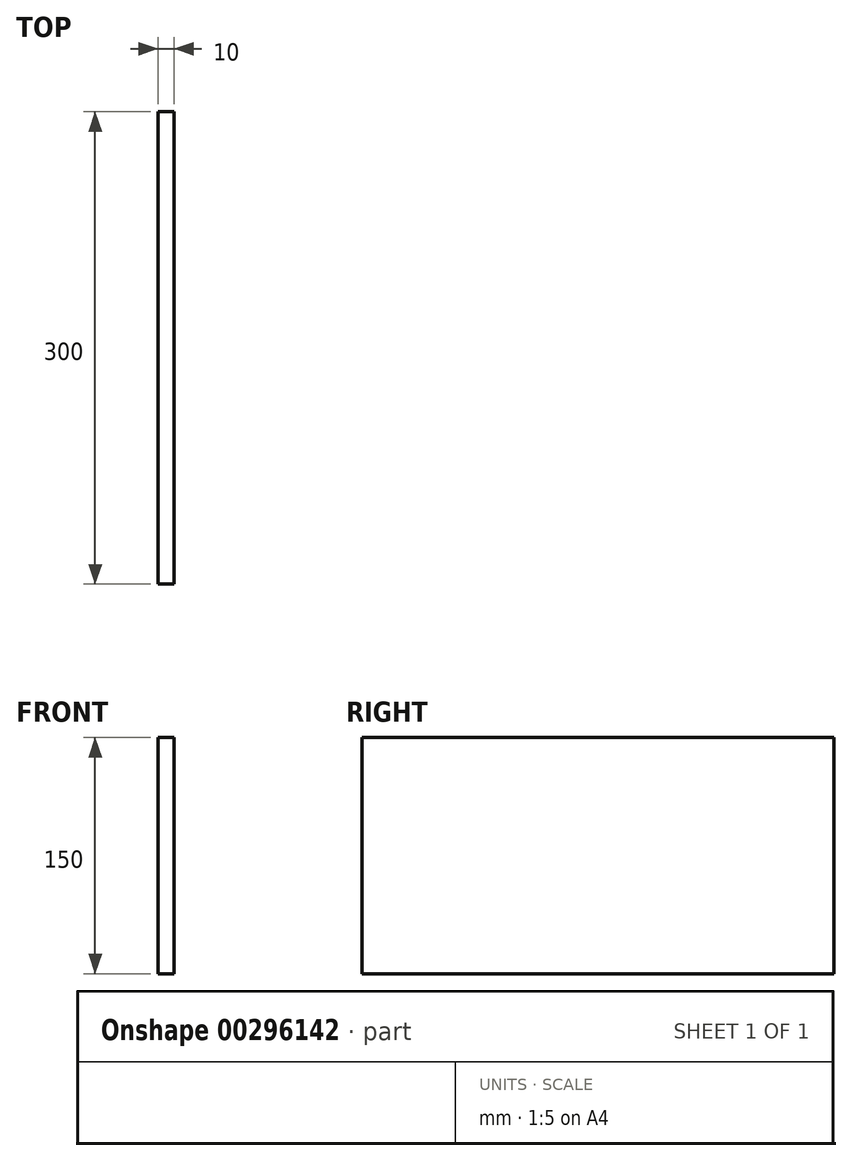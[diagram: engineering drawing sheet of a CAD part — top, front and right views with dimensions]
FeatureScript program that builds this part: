
annotation { "Feature Type Name" : "Feature", "Feature Type Description" : "" }
export const myFeature = defineFeature(function(context is Context, id is Id, definition is map)
    precondition{}
    {
        {
            var Q0;
            Q0=qCreatedBy(makeId("Front.planeOp"),FACE);
            var sketch = newSketch(context, id + "F0", { "sketchPlane" : qUnion([Q0])});
            skLineSegment(sketch, "E0.bottom", {"start": v(5, 75) * mm, "end": v(-5, 75) * mm});
            skLineSegment(sketch, "E0.top", {"start": v(5, -75) * mm, "end": v(-5, -75) * mm});
            skLineSegment(sketch, "E0.left", {"start": v(5, 75) * mm, "end": v(5, -75) * mm});
            skLineSegment(sketch, "E0.right", {"start": v(-5, 75) * mm, "end": v(-5, -75) * mm});
            skPoint(sketch, "E0.middle", {"position": v(0, 0) * mm});
            skSolve(sketch);
        }
        {
            var Q0;
            Q0=qSketchRegion(id+"F0",true);
            extrude(context, id + "F1", {"entities" : qUnion([Q0]), "oppositeDirection" : true, "depth" : 300 * mm});
        }
    });
